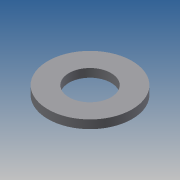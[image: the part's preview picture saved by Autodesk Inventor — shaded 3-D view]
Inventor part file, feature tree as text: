
AUTODESK INVENTOR PART (.ipt)
format: ipt  version: 2013 (Build 170138000, 138)  size: 72,704 bytes
history: native  units: mm
features: extrude x1, sketch x1
ambient origin geometry x8: Origin, YZ Plane, XZ Plane, XY Plane, X Axis, Y Axis, Z Axis, Center Point
bodies: Solid1 (feature_tree)
feature tree (2):
  extrude  "Extrusion1"  Depth=10.0mm
  sketch  "Sketch1"  dims[d0=5.0mm d2=10.0mm d3=1.0mm d4=0.0mm]
